# Revit family: Magnuson-Office-Racks
name_source: partatom
category: Furniture
revit_build: Autodesk Revit 2014 (Build: 20140709_2115(x64)
units: mm (PartAtom-declared; Revit-internal decimal feet)

## types (6) — shared parameters
Assembly Code = E2020200
Depth = 18.5 "
GLIDE = MG - UHMW, Black
HANGER = MG - UHMW, Black
Height = 60 "
Keynote = 12500
Manufacturer = MAGNUSON GROUP
RACK = MG - Paint
Type Comments = OFFICE RAK
UR = Yes
URL = www.magnusongrouop.com

## per-type parameters (varying)
| type | BR | Description | Hanger Distance | Hanger No | Rail Gap | UB | UR No | Upper Rack No | Width |
| 3D-OR-2A | Yes | 24"x18.5" Mobile Rack, With Hat Shelf, Umbrella Holder, Boot Shelf | 2.895 " | 8 | 3 " | Yes | 23 | 8 | 24 " |
| 3D-OR-2B | No | 24"x18.5" Mobile Rack, With Hat Shelf, | 2.895 " | 8 | 2.75 " | No | 23 | 2 | 24 " |
| 3D-OR-3A | Yes | 36"x18.5" Mobile Rack, With Hat Shelf, Umbrella Holder, Boot Shelf | 5.79 " | 6 | 3 " | Yes | 35 | 12 | 36 " |
| 3D-OR-3B | No | 36"x18.5" Mobile Rack, With Hat Shelf, | 5.79 " | 6 | 2.75 " | No | 35 | 3 | 36 " |
| 3D-OR-4A | Yes | 48"x18.5" Mobile Rack, With Hat Shelf, Umbrella Holder, Boot Shelf | 5.79 " | 8 | 3 " | Yes | 47 | 16 | 48 " |
| 3D-OR-4B | No | 48"x18.5" Mobile Rack, With Hat Shelf, | 5.79 " | 8 | 2.75 " | No | 47 | 4 | 48 " |

note: column(s) folded — value = type name in every type: Model

## geometry (parser evidence)
native form markers: Sweep x10
no freeform markers — native parametric forms only
